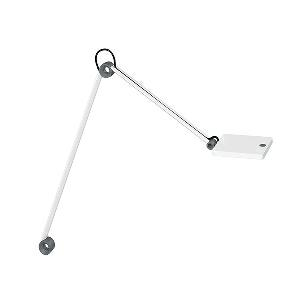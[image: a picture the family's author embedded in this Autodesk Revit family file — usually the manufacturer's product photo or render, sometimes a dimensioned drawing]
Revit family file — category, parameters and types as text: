
# Revit family: para_mi_-_ftl_108_r__940_00638510_1e7d
name_source: partatom
category: Lighting Fixtures
units: mm (PartAtom-declared; Revit-internal decimal feet)

## family parameters
Cut with Voids When Loaded = No
Host = Face
Light Source = No
Part Type = Normal
Room Calculation Point = No
Round Connector Dimension = Use Diameter
Shared = No

## types (1)
- PARA.MI - FTL 108 R /940 (1 x LED, 600 lm, 4000K)
    Apparent Load = 7 VA
    Approval mark = CE
    CIE Flux Codes = 70 94 99 100 100
    Color Rendering = 90-100
    Color Temperature = 4000K
    Control Gear = Electronic ballast
    Default Elevation = 1800 mm
    Description = FTL 108 R|Task luminaire|light source: LED|work equipment: Electronic plug-in transformer|connected load: 100-240 V, 50/60 Hz|Power consumption: approx. 7 W|luminous flux: 600 lm|luminous efficacy: 85 lm/W|Illuminance efficiency factor: 111 lx/W|colour temperature: Cold white, ca. 4000 K|color rendering index (CRI): >= 90|chromaticity tolerance:  3 SDCM|class of protection: II with plug-in power supply, III without plug-in power supply|technology: Continuously dimmable|luminaire body|material: Aluminium|surface: Painted|colour: White|lamp cover: Plastic, Clear|tubular sections|material: Tubular aluminium section|surface: Painted|colour: White|weight (net): approx. 1.0 kg|mains lead: 3.00 m Mains plug BS 1363, CEE 7/XVI, NEMA 1-15P|Fastening: Adaptor (accessory), Table base (accessory), Table clamp (accessory), Tap16|glare control: Reflector|special features: Automatic switchoff adjustable, Push button in luminaire head, Behaviour at net recovery adjustable|Approval mark: C - ETL - US (F. CAN U. USA), VDE - ENEC SEP LIGHT & POWER SUPPLY UNIT|
    Height = 12 mm  [stored 0.0393701 ft]
    Lamp = 1 x LED
    Lamp Light Flux = 600 lm
    Lamp count = 1
    Length = 123 mm
    Luminous efficacy = 86 lm/W
    Manufacturer = Waldmann
    ModVariant = No
    Model = 00638510
    Mounting Place = Table
    Mounting Type = Surface mounted
    Number of Poles = 1
    OnlyDefault = Yes
    Power Factor = 1
    Product Name = PARA.MI - FTL 108 R /940
    Product group = Task luminaire (office)
    ProductGroupID = 21
    Protection Class = Protection class II
    Protection Degree = IP 40
    RLX_Detail_Level = 1
    RLX_Emergency_Light_Flux = 0 lm
    RLX_Emergency_Type = 0
    RLX_Emergency_Type_DB = No
    RlxData = <blob elided: 68485 chars, md5=1b75969d>
    Socket = socket
    Standby Power = 0 W
    System Light Flux = 600 lm
    System Power = 7 W
    Type Comments = Product without accessories
    Type Image = 113148000-00638510.jpg
    URL = http://relux.com
    VarID = ---
    Voltage = 230 V
    Voltage Range = 220-240 V
    Weight = 0.00 kg
    Width = 0 mm  [stored 0 ft]

note: [stored X ft] marks values corroborated as IEEE doubles in the binary element streams (Revit-internal decimal feet)

## geometry (parser evidence)
native form markers: Blend x4, Sweep x13
no freeform markers — native parametric forms only
